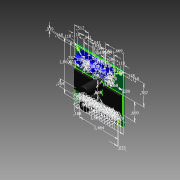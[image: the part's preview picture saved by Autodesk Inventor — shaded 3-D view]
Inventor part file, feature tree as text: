
AUTODESK INVENTOR PART (.ipt)
format: ipt  version: 2012 (Build 160160000, 160)  size: 497,152 bytes
history: native  units: in
note: dims shown in document units (in); Inventor stores cm internally (conversion verified against a paired STEP export)
features: extrude x11, fillet x3, sketch x2, chamfer x2
ambient origin geometry x8: Origin, YZ Plane, XZ Plane, XY Plane, X Axis, Y Axis, Z Axis, Center Point
bodies: Solid1 (feature_tree)
feature tree (18):
  sketch  "Sketch1"  dims[d0=1.86in d1=1.86in]
  extrude  "Extrusion1"  Depth=1.86in
  extrude  "Extrusion2"  Depth=0.1181in
  extrude  "Extrusion3"  Depth=0.1181in
  extrude  "Extrusion4"  Depth=0.1181in
  extrude  "Extrusion5"  Depth=0.1181in
  extrude  "Extrusion6"  Depth=0.1181in
  fillet  "Fillet1"  Radius=1.1811in
  fillet  "Fillet2"  Radius=0.3937in
  chamfer  "Chamfer1"  Distance=0.3937in
  chamfer  "Chamfer2"  Distance=0.3394in
  extrude  "Extrusion7"  Depth=0.0394in
  extrude  "Extrusion8"  Depth=0.2953in
  extrude  "Extrusion9"  Depth=1.4843in
  fillet  "Fillet3"  Radius=0.188in
  extrude  "Extrusion10"  Depth=0.6693in
  extrude  "Extrusion11"  Depth=0.6693in
  sketch  "Sketch2"  dims[d2=0.1181in d3=0.1181in d4=0.1181in d5=0.1181in d6=0.1181in d7=0.1181in d8=1.1811in d9=0.3937in d10=0.3937in d11=0.3394in d12=0.0394in d13=0.2953in d14=1.4843in d15=0.188in d16=0.6693in d17=0.6693in d18=0.6693in d19=0.6693in d20=0.7874in d21=0.7874in d23=0.0197in d24=0.0197in d25=0.0197in d26=0.0197in d27=0.0197in d28=0.0197in d29=0.0197in d30=0.0197in d31=0.0197in d32=0.0197in d33=0.0197in d34=0.0197in d35=0.0197in d36=0.0197in d37=0.0197in d38=0.0197in d39=0.0197in d40=0.0197in d41=0.0197in d42=0.0197in d43=0.0197in d44=0.0197in d45=0.0197in d46=0.0197in d47=0.0197in d48=0.0197in d49=0.0197in d50=0.0197in d51=0.0197in d52=0.0197in d53=0.0325in d54=0.1in d55=0.1in d56=0.1in d57=0.1in d58=0.1in d59=0.1in d60=0.1in d61=0.1in d62=0.1in d63=0.1in d64=0.1in d65=0.1in d66=0.1in d67=0.0999in d68=0.0394in d69=0.0394in d70=0.3937in d71=0.3937in d72=0.1181in d73=0.1181in d74=0.1181in d75=0.1181in d76=0.1181in d77=0.1181in d78=0.041in d79=0.041in d80=0.041in d81=0.041in d82=0.041in d83=0.041in d84=0.0984in d85=0.0in d86=0.2953in d87=0.0in d88=0.0984in d89=0.0395in d90=0.0395in d91=0.0395in d92=0.0395in d93=0.0395in d94=0.0395in d95=0.0395in d96=0.0395in d97=0.0395in d98=0.0395in d99=0.0395in d100=0.0395in d101=0.0395in d102=0.0395in d103=0.0395in d104=0.2643in d105=0.0787in d106=0.0in d107=0.3937in d108=0.0in d109=0.2953in d110=0.0in d111=0.5906in d112=0.0in d113=0.02in d114=0.01in d115=0.07in d116=0.125in d117=60.0deg d118=0.04in d119=0.125in d120=0.481in d121=0.0394in d122=0.0394in d123=0.0394in d124=0.0394in d125=0.0394in d126=0.1575in d127=0.1575in d128=0.1575in d129=0.1575in d130=0.1575in d131=0.1575in d132=0.1969in d133=0.1969in d134=0.1969in d135=0.1969in d136=0.1969in d137=0.1969in d138=0.0435in d139=0.0435in d140=0.0435in d141=0.0435in d142=0.0435in d143=0.0435in d144=0.0197in d145=0.2362in d146=0.0in d147=0.063in d148=0.0in d149=0.2362in d150=0.2362in d151=0.2362in d152=0.2362in d153=0.5118in d154=0.6693in d155=0.0394in d156=0.0394in d157=0.0984in d158=-0.0in d159=0.01in d160=0.09in d161=0.09in d162=0.13in d163=0.13in d164=0.04in d165=0.04in d166=0.02in d167=0.02in d168=0.04in d169=0.13in d170=0.13in d171=0.04in d172=0.04in d173=0.04in d174=0.02in d175=0.02in d176=0.0394in d177=0.0in d178=0.0197in d179=0.0in]
